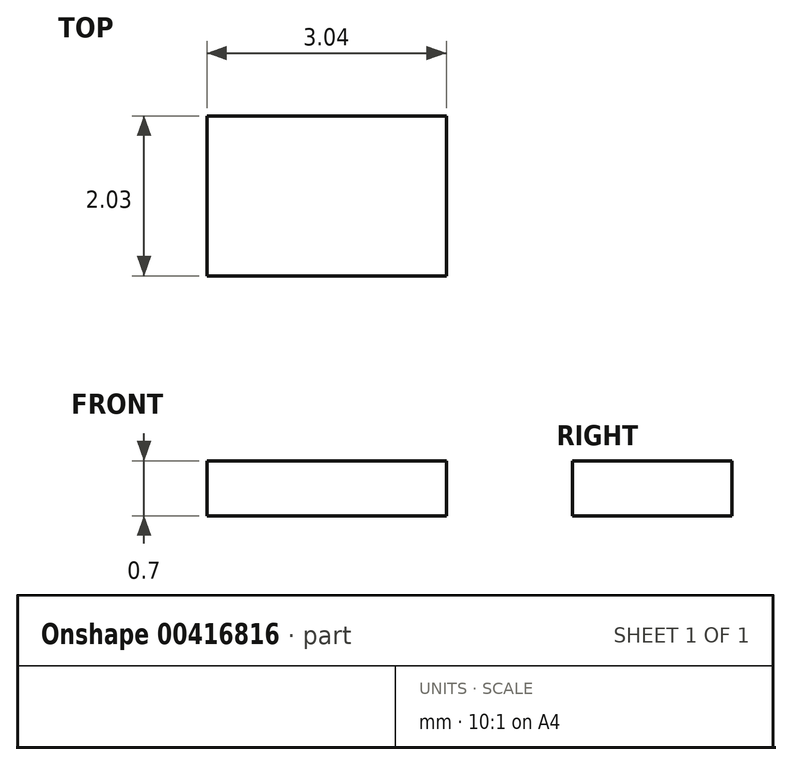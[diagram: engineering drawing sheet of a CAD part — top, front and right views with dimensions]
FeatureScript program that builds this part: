
annotation { "Feature Type Name" : "Feature", "Feature Type Description" : "" }
export const myFeature = defineFeature(function(context is Context, id is Id, definition is map)
    precondition{}
    {
        {
            var Q0;
            Q0=qCreatedBy(makeId("Top.planeOp"),FACE);
            var sketch = newSketch(context, id + "F0", { "sketchPlane" : qUnion([Q0])});
            skLineSegment(sketch, "E0.bottom", {"start": v(0, 0) * mm, "end": v(3.04, 0) * mm});
            skLineSegment(sketch, "E0.top", {"start": v(0, 2.03) * mm, "end": v(3.04, 2.03) * mm});
            skLineSegment(sketch, "E0.left", {"start": v(0, 0) * mm, "end": v(0, 2.03) * mm});
            skLineSegment(sketch, "E0.right", {"start": v(3.04, 0) * mm, "end": v(3.04, 2.03) * mm});
            skSolve(sketch);
        }
        {
            var Q0;
            Q0 = qSketchRegion(id + "F0", true);
            extrude(context, id + "F1", {"entities" : qUnion([Q0]), "depth" : .7 * mm, "offsetDistance" : 25.4 * mm});
        }
    });
